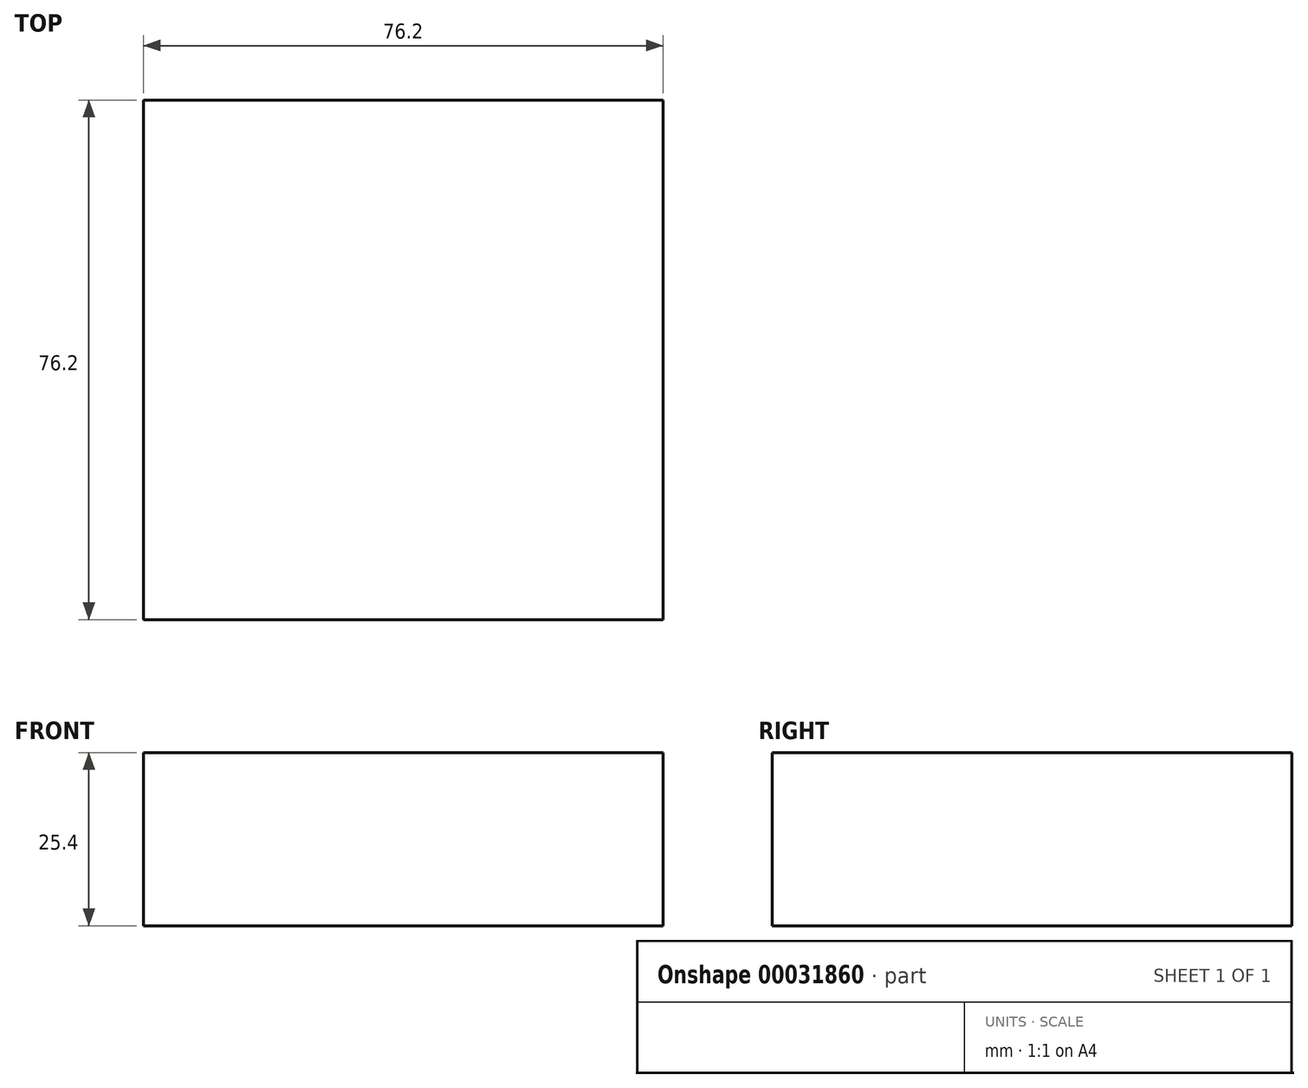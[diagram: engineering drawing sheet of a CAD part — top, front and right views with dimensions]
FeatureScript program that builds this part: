
annotation { "Feature Type Name" : "Feature", "Feature Type Description" : "" }
export const myFeature = defineFeature(function(context is Context, id is Id, definition is map)
    precondition{}
    {
        {
            var Q0;
            Q0=qCreatedBy(makeId("Top.planeOp"),FACE);
            var sketch = newSketch(context, id + "F0", { "sketchPlane" : qUnion([Q0])});
            skLineSegment(sketch, "E0.bottom", {"start": v(-57.83, 37.74) * mm, "end": v(18.37, 37.74) * mm});
            skLineSegment(sketch, "E0.top", {"start": v(-57.83, -38.46) * mm, "end": v(18.37, -38.46) * mm});
            skLineSegment(sketch, "E0.left", {"start": v(-57.83, 37.74) * mm, "end": v(-57.83, -38.46) * mm});
            skLineSegment(sketch, "E0.right", {"start": v(18.37, 37.74) * mm, "end": v(18.37, -38.46) * mm});
            skSolve(sketch);
        }
        {
            var Q0;
            Q0 = qSketchRegion(id + "F0", true);
            extrude(context, id + "F1", {"entities" : qUnion([Q0]), "depth" : 25.4 * mm});
        }
    });
